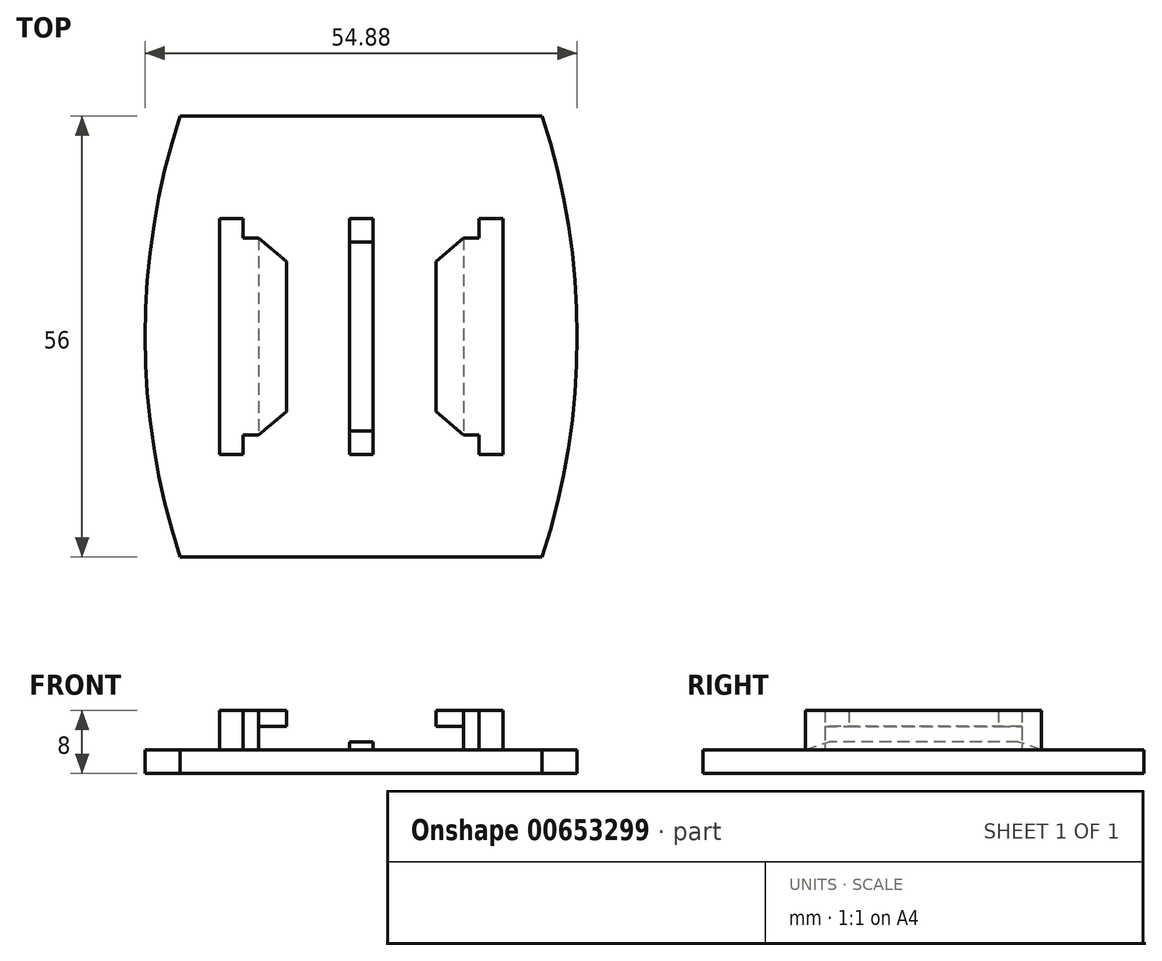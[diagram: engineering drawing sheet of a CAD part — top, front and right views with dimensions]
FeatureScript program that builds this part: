
annotation { "Feature Type Name" : "Feature", "Feature Type Description" : "" }
export const myFeature = defineFeature(function(context is Context, id is Id, definition is map)
    precondition{}
    {
        {
            var Q0;
            Q0=qCreatedBy(makeId("Top.planeOp"),FACE);
            var sketch = newSketch(context, id + "F0", { "sketchPlane" : qUnion([Q0])});
            skLineSegment(sketch, "E0.bottom", {"start": v(0, 0) * mm, "end": v(-46, 0) * mm});
            skLineSegment(sketch, "E0.top", {"start": v(0, -56) * mm, "end": v(-46, -56) * mm});
            skArc(sketch, "E1", {"start": v(-46, 0) * mm, "mid": v(-50.44, -28) * mm, "end": v(-46, -56) * mm});
            skArc(sketch, "E2.trimOffspring", {"start": v(0, -56) * mm, "mid": v(4.44, -28) * mm, "end": v(0, 0) * mm});
            skSolve(sketch);
        }
        {
            var Q0;
            Q0=qSketchRegion(id+"F0",true);
            extrude(context, id + "F1", {"entities" : qUnion([Q0]), "depth" : 3 * mm});
        }
        {
            var Q0;
            Q0=makeQuery(id+"F1.opExtrude","CAP_FACE",FACE,{"disambiguationData":[OSD([sQuery(id+"F0.wireOp",EDGE,"E0.bottom"),sQuery(id+"F0.wireOp",EDGE,"E0.top"),sQuery(id+"F0.wireOp",EDGE,"E0.left"),sQuery(id+"F0.wireOp",EDGE,"E0.right")])],"isStart":false});
            var sketch = newSketch(context, id + "F2", { "sketchPlane" : qUnion([Q0])});
            skLineSegment(sketch, "E3.bottom", {"start": v(-41, -13) * mm, "end": v(-38, -13) * mm});
            skLineSegment(sketch, "E3.top", {"start": v(-41, -43) * mm, "end": v(-38, -43) * mm});
            skLineSegment(sketch, "E3.left", {"start": v(-41, -13) * mm, "end": v(-41, -43) * mm});
            skLineSegment(sketch, "E3.right", {"start": v(-38, -13) * mm, "end": v(-38, -15.5) * mm});
            skLineSegment(sketch, "E4.bottom", {"start": v(-38, -15.5) * mm, "end": v(-36, -15.5) * mm});
            skLineSegment(sketch, "E4.top", {"start": v(-38, -40.5) * mm, "end": v(-36, -40.5) * mm});
            skLineSegment(sketch, "E4.right", {"start": v(-36, -15.5) * mm, "end": v(-36, -40.5) * mm});
            skLineSegment(sketch, "E5.bottom", {"start": v(-5, -13) * mm, "end": v(-8, -13) * mm});
            skLineSegment(sketch, "E5.top", {"start": v(-5, -43) * mm, "end": v(-8, -43) * mm});
            skLineSegment(sketch, "E5.left", {"start": v(-5, -13) * mm, "end": v(-5, -43) * mm});
            skLineSegment(sketch, "E5.right", {"start": v(-8, -13) * mm, "end": v(-8, -15.5) * mm});
            skLineSegment(sketch, "E6.bottom", {"start": v(-8, -15.5) * mm, "end": v(-10, -15.5) * mm});
            skLineSegment(sketch, "E6.top", {"start": v(-8, -40.5) * mm, "end": v(-10, -40.5) * mm});
            skLineSegment(sketch, "E6.right", {"start": v(-10, -15.5) * mm, "end": v(-10, -40.5) * mm});
            skLineSegment(sketch, "E7.trimOffspring", {"start": v(-38, -40.5) * mm, "end": v(-38, -43) * mm});
            skLineSegment(sketch, "E8.trimOffspring", {"start": v(-8, -40.5) * mm, "end": v(-8, -43) * mm});
            skSolve(sketch);
        }
        {
            var Q0;
            Q0=qSketchRegion(id+"F2",true);
            extrude(context, id + "F3", {"entities" : qUnion([Q0]), "operationType" : NewBodyOperationType.ADD, "depth" : 3 * mm, "offsetDistance" : 25 * mm});
        }
        {
            var Q0;
            Q0=makeQuery(id+"F3.opExtrude","CAP_FACE",FACE,{"disambiguationData":[OSD([sQuery(id+"F2.wireOp",EDGE,"E3.bottom"),sQuery(id+"F2.wireOp",EDGE,"E3.top"),sQuery(id+"F2.wireOp",EDGE,"E3.left"),sQuery(id+"F2.wireOp",EDGE,"E3.right"),sQuery(id+"F2.wireOp",EDGE,"E4.bottom"),sQuery(id+"F2.wireOp",EDGE,"E4.top"),sQuery(id+"F2.wireOp",EDGE,"E4.right"),sQuery(id+"F2.wireOp",EDGE,"E7.trimOffspring")])],"isStart":false});
            var sketch = newSketch(context, id + "F4", { "sketchPlane" : qUnion([Q0])});
            skLineSegment(sketch, "E9", {"start": v(-41, -13) * mm, "end": v(-41, -43) * mm});
            skLineSegment(sketch, "E10", {"start": v(-41, -43) * mm, "end": v(-38, -43) * mm});
            skLineSegment(sketch, "E11", {"start": v(-38, -43) * mm, "end": v(-38, -40.5) * mm});
            skLineSegment(sketch, "E12", {"start": v(-38, -40.5) * mm, "end": v(-36, -40.5) * mm});
            skLineSegment(sketch, "E13", {"start": v(-36, -40.5) * mm, "end": v(-32.5, -37.5) * mm});
            skLineSegment(sketch, "E14", {"start": v(-32.5, -37.5) * mm, "end": v(-32.5, -18.5) * mm});
            skLineSegment(sketch, "E15", {"start": v(-32.5, -18.5) * mm, "end": v(-36, -15.5) * mm});
            skLineSegment(sketch, "E16", {"start": v(-36, -15.5) * mm, "end": v(-38, -15.5) * mm});
            skLineSegment(sketch, "E17", {"start": v(-38, -15.5) * mm, "end": v(-38, -13) * mm});
            skLineSegment(sketch, "E18", {"start": v(-38, -13) * mm, "end": v(-41, -13) * mm});
            skSolve(sketch);
        }
        {
            var Q0;
            Q0=qSketchRegion(id+"F4",true);
            extrude(context, id + "F5", {"entities" : qUnion([Q0]), "operationType" : NewBodyOperationType.ADD, "depth" : 2 * mm});
        }
        {
            var Q0;
            Q0=makeQuery(id+"F3.opExtrude","CAP_FACE",FACE,{"disambiguationData":[OSD([sQuery(id+"F2.wireOp",EDGE,"E5.bottom"),sQuery(id+"F2.wireOp",EDGE,"E5.top"),sQuery(id+"F2.wireOp",EDGE,"E5.left"),sQuery(id+"F2.wireOp",EDGE,"E5.right"),sQuery(id+"F2.wireOp",EDGE,"E6.bottom"),sQuery(id+"F2.wireOp",EDGE,"E6.top"),sQuery(id+"F2.wireOp",EDGE,"E6.right"),sQuery(id+"F2.wireOp",EDGE,"E8.trimOffspring")])],"isStart":false});
            var sketch = newSketch(context, id + "F6", { "sketchPlane" : qUnion([Q0])});
            skLineSegment(sketch, "E19", {"start": v(-8, -13) * mm, "end": v(-8, -15.5) * mm});
            skLineSegment(sketch, "E20", {"start": v(-8, -15.5) * mm, "end": v(-10, -15.5) * mm});
            skLineSegment(sketch, "E21", {"start": v(-10, -15.5) * mm, "end": v(-13.5, -18.5) * mm});
            skLineSegment(sketch, "E22", {"start": v(-13.5, -18.5) * mm, "end": v(-13.5, -37.5) * mm});
            skLineSegment(sketch, "E23", {"start": v(-13.5, -37.5) * mm, "end": v(-10, -40.5) * mm});
            skLineSegment(sketch, "E24", {"start": v(-10, -40.5) * mm, "end": v(-8, -40.5) * mm});
            skLineSegment(sketch, "E25", {"start": v(-8, -40.5) * mm, "end": v(-8, -43) * mm});
            skLineSegment(sketch, "E26", {"start": v(-8, -43) * mm, "end": v(-5, -43) * mm});
            skLineSegment(sketch, "E27", {"start": v(-5, -43) * mm, "end": v(-5, -13) * mm});
            skLineSegment(sketch, "E28", {"start": v(-5, -13) * mm, "end": v(-8, -13) * mm});
            skSolve(sketch);
        }
        {
            var Q0;
            Q0=qSketchRegion(id+"F6",true);
            extrude(context, id + "F7", {"entities" : qUnion([Q0]), "operationType" : NewBodyOperationType.ADD, "depth" : 2 * mm});
        }
        {
            var Q0;
            Q0=makeQuery(id+"F1.opExtrude","CAP_FACE",FACE,{"disambiguationData":[OSD([sQuery(id+"F0.wireOp",EDGE,"E0.bottom"),sQuery(id+"F0.wireOp",EDGE,"E0.top"),sQuery(id+"F0.wireOp",EDGE,"E0.left"),sQuery(id+"F0.wireOp",EDGE,"E0.right")])],"isStart":false});
            var sketch = newSketch(context, id + "F8", { "sketchPlane" : qUnion([Q0])});
            skLineSegment(sketch, "E29.bottom", {"start": v(-24.5, -13) * mm, "end": v(-21.5, -13) * mm});
            skLineSegment(sketch, "E29.top", {"start": v(-24.5, -43) * mm, "end": v(-21.5, -43) * mm});
            skLineSegment(sketch, "E29.left", {"start": v(-24.5, -13) * mm, "end": v(-24.5, -43) * mm});
            skLineSegment(sketch, "E29.right", {"start": v(-21.5, -13) * mm, "end": v(-21.5, -43) * mm});
            skSolve(sketch);
        }
        {
            var Q0;
            Q0=qSketchRegion(id+"F8",true);
            extrude(context, id + "F9", {"entities" : qUnion([Q0]), "operationType" : NewBodyOperationType.ADD, "depth" : 1 * mm});
        }
        {
            var Q0;
            Q0=makeQuery(id+"F9.opExtrude","CAP_EDGE",EDGE,{"disambiguationData":[OSD([sQuery(id+"F8.wireOp",EDGE,"E29.bottom")])],"isStart":false});
            var Q1;
            Q1=makeQuery(id+"F9.opExtrude","CAP_EDGE",EDGE,{"disambiguationData":[OSD([sQuery(id+"F8.wireOp",EDGE,"E29.top")])],"isStart":false});
            chamfer(context, id + "F10", {"entities" : qUnion([Q0, Q1]), "chamferType" : ChamferType.TWO_OFFSETS, "width1" : 1 * mm, "oppositeDirection" : false, "width2" : 3 * mm, "tangentPropagation" : true});
        }
    });
